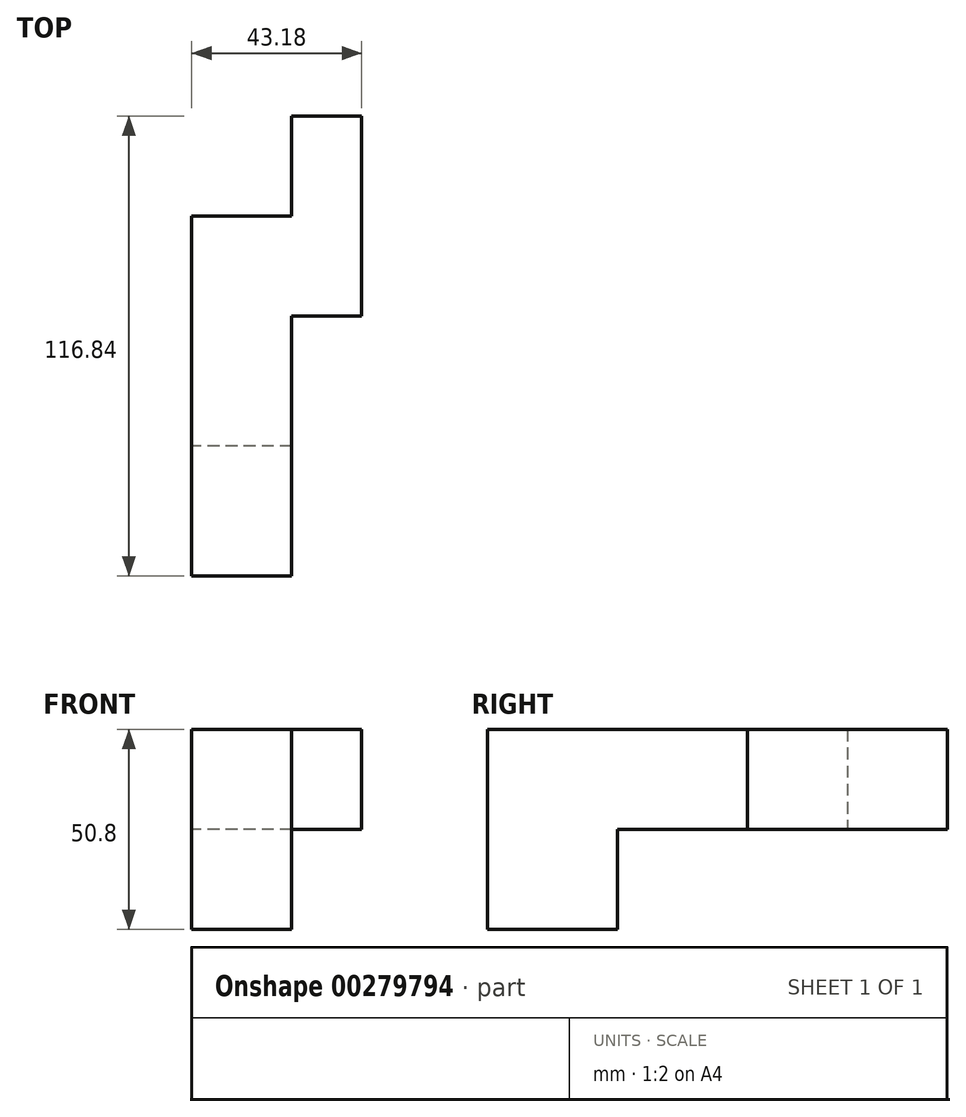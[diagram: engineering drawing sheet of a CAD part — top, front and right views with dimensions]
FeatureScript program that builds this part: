
annotation { "Feature Type Name" : "Feature", "Feature Type Description" : "" }
export const myFeature = defineFeature(function(context is Context, id is Id, definition is map)
    precondition{}
    {
        {
            var Q0;
            Q0=qCreatedBy(makeId("Right.planeOp"),FACE);
            var sketch = newSketch(context, id + "F0", { "sketchPlane" : qUnion([Q0])});
            skLineSegment(sketch, "E0.bottom", {"start": v(71.07, -13.6) * mm, "end": v(20.27, -13.6) * mm});
            skLineSegment(sketch, "E0.top", {"start": v(71.07, -39) * mm, "end": v(20.27, -39) * mm});
            skLineSegment(sketch, "E0.left", {"start": v(71.07, -13.6) * mm, "end": v(71.07, -39) * mm});
            skLineSegment(sketch, "E0.right", {"start": v(20.27, -13.6) * mm, "end": v(20.27, -39) * mm});
            skLineSegment(sketch, "E1", {"start": v(45.67, -13.6) * mm, "end": v(45.67, -39) * mm});
            skSolve(sketch);
        }
        {
            var Q0;
            {var subQ0=sQuery(id+"F0.wireOp",EDGE,"E0.left");Q0=makeQuery(id+"F0.imprint","IMPRINT",FACE,{"disambiguationData":[TD([[makeQuery(id+"F0.imprint","IMPRINT",EDGE,{"derivedFrom":subQ0}),-1.0]])]});}
            extrude(context, id + "F1", {"entities" : qUnion([Q0]), "oppositeDirection" : true, "depth" : 17.78 * mm});
        }
        {
            var Q0;
            {var subQ0=sQuery(id+"F0.wireOp",EDGE,"E0.right");Q0=makeQuery(id+"F0.imprint","IMPRINT",FACE,{"disambiguationData":[TD([[makeQuery(id+"F0.imprint","IMPRINT",EDGE,{"derivedFrom":subQ0}),1.0]])]});}
            extrude(context, id + "F2", {"entities" : qUnion([Q0]), "operationType" : NewBodyOperationType.ADD, "oppositeDirection" : true, "depth" : 43.18 * mm});
        }
        {
            var Q0;
            Q0=makeQuery(id+"F2.opExtrude","SWEPT_FACE",FACE,{"disambiguationData":[OSD([sQuery(id+"F0.wireOp",EDGE,"E0.right")])]});
            var sketch = newSketch(context, id + "F3", { "sketchPlane" : qUnion([Q0])});
            skLineSegment(sketch, "E2", {"start": v(-17.78, -13.6) * mm, "end": v(-17.78, -39) * mm});
            skSolve(sketch);
        }
        {
            var Q0;
            {var subQ0=sQuery(id+"F3.wireOp",EDGE,"E2");Q0=makeQuery(id+"F3.imprint","IMPRINT",FACE,{"disambiguationData":[TD([[makeQuery(id+"F3.imprint","IMPRINT",EDGE,{"derivedFrom":subQ0}),-1.0]])]});}
            extrude(context, id + "F4", {"entities" : qUnion([Q0]), "operationType" : NewBodyOperationType.ADD, "depth" : 66.04 * mm});
        }
        {
            var Q0;
            {var subQ0=sQuery(id+"F0.wireOp",EDGE,"E0.top");Q0=makeQuery(id+"F4.boolean.opBoolean","MERGE",FACE,{"derivedFrom":[makeQuery(id+"F2.boolean.opBoolean","MERGE",FACE,{"derivedFrom":[makeQuery(id+"F1.opExtrude","SWEPT_FACE",FACE,{"disambiguationData":[OSD([subQ0])]}),makeQuery(id+"F2.opExtrude","SWEPT_FACE",FACE,{"disambiguationData":[OSD([subQ0])]})]}),makeQuery(id+"F4.opExtrude","SWEPT_FACE",FACE,{"disambiguationData":[OSD([subQ0,sQuery(id+"F0.wireOp",EDGE,"E0.right")])]})]});}
            var sketch = newSketch(context, id + "F5", { "sketchPlane" : qUnion([Q0])});
            skLineSegment(sketch, "E3", {"start": v(-17.78, 12.75) * mm, "end": v(-43.18, 12.75) * mm});
            skSolve(sketch);
        }
        {
            var Q0;
            {var subQ0=sQuery(id+"F5.wireOp",EDGE,"E3");Q0=makeQuery(id+"F5.imprint","IMPRINT",FACE,{"disambiguationData":[TD([[makeQuery(id+"F5.imprint","IMPRINT",EDGE,{"derivedFrom":subQ0}),-1.0]])]});}
            extrude(context, id + "F6", {"entities" : qUnion([Q0]), "operationType" : NewBodyOperationType.ADD, "depth" : 25.4 * mm});
        }
    });
